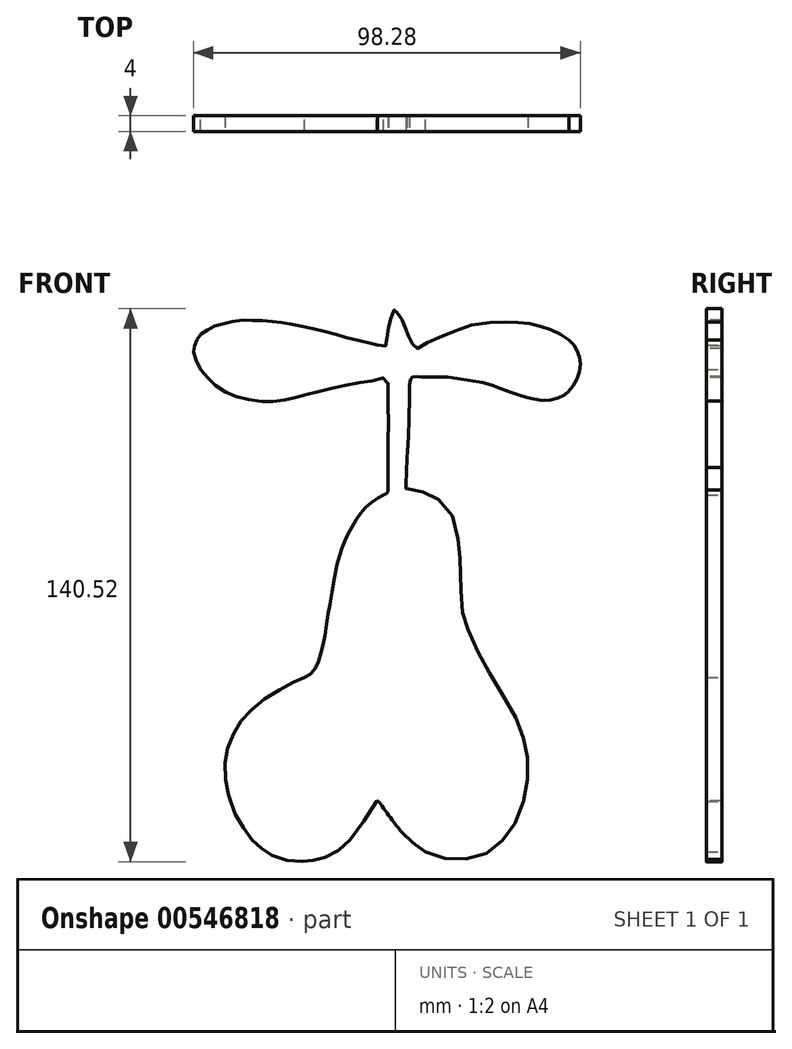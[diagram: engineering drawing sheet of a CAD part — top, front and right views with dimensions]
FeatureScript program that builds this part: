
annotation { "Feature Type Name" : "Feature", "Feature Type Description" : "" }
export const myFeature = defineFeature(function(context is Context, id is Id, definition is map)
    precondition{}
    {
        {
            var Q0;
            Q0=qCreatedBy(makeId("Front.planeOp"),FACE);
            var sketch = newSketch(context, id + "F0", { "sketchPlane" : qUnion([Q0])});
            skFitSpline(sketch, "E0", {"points": [v(-20.35, -65.57) * mm, v(-23.14, -70.04) * mm, v(-26.51, -74.67) * mm, v(-28.55, -76.95) * mm, v(-30.23, -78.14) * mm, v(-32.67, -79.37) * mm, v(-33.78, -79.88) * mm, v(-35.11, -80.2) * mm, v(-36.93, -80.61) * mm, v(-38.53, -80.75) * mm, v(-39.07, -80.8) * mm, v(-40.43, -80.88) * mm, v(-43.22, -80.56) * mm, v(-45.88, -79.83) * mm, v(-47.46, -78.88) * mm, v(-48.54, -78.2) * mm, v(-50.17, -76.95) * mm, v(-51.26, -75.97) * mm, v(-52.29, -74.89) * mm, v(-53.54, -73.2) * mm, v(-55, -71) * mm, v(-56.38, -68.51) * mm, v(-57.66, -64.74) * mm, v(-58.37, -62) * mm, v(-58.72, -59.5) * mm, v(-58.83, -56.87) * mm, v(-58.64, -54.6) * mm, v(-58.23, -52.48) * mm, v(-57.74, -50.77) * mm, v(-56.41, -47.97) * mm, v(-55.22, -45.88) * mm, v(-54.19, -44.58) * mm, v(-52.56, -42.87) * mm, v(-50.44, -40.8) * mm, v(-48.22, -39.2) * mm, v(-45.56, -37.6) * mm, v(-43.3, -36.3) * mm, v(-41.3, -35.27) * mm, v(-39.72, -34.57) * mm, v(-38.58, -34.08) * mm], "startDerivative": vector(-67.21, -112.45) * mm, "endDerivative": vector(58.14, 24.82) * mm});
            skFitSpline(sketch, "E1", {"points": [v(-38.58, -34.08) * mm, v(-37.08, -33.12) * mm, v(-35.5, -31.05) * mm, v(-34.4, -27.64) * mm, v(-33.66, -24.6) * mm, v(-32.78, -19.2) * mm, v(-32.01, -14.78) * mm, v(-30.44, -6) * mm, v(-29.4, -2.35) * mm, v(-28.44, 0.5) * mm, v(-27.37, 2.68) * mm, v(-25.95, 5.33) * mm, v(-24.34, 7.7) * mm, v(-22.5, 9.62) * mm, v(-20.2, 11.35) * mm, v(-18.58, 12.35) * mm], "startDerivative": vector(31.4, 16.8) * mm, "endDerivative": vector(30.53, 18.13) * mm});
            skFitSpline(sketch, "E2", {"points": [v(-18.58, 12.35) * mm, v(-17.6, 12.81) * mm, v(-17.35, 13.9) * mm, v(-17.33, 15.7) * mm], "startDerivative": vector(3.83, 1.07) * mm, "endDerivative": vector(0, 4.79) * mm});
            skFitSpline(sketch, "E3", {"points": [v(-17.33, 15.7) * mm, v(-17.33, 25.86) * mm, v(-17.33, 33.69) * mm, v(-17.33, 38.6) * mm, v(-17.33, 40.37) * mm, v(-17.96, 41.98) * mm, v(-20.9, 41.44) * mm, v(-23.99, 40.9) * mm, v(-29.9, 39.75) * mm, v(-33.54, 38.98) * mm, v(-37.55, 37.91) * mm, v(-40.6, 37.14) * mm, v(-43.8, 36.38) * mm, v(-47.05, 36.07) * mm, v(-50.25, 36.15) * mm, v(-54.7, 36.99) * mm, v(-57.9, 38.06) * mm, v(-60.83, 39.9) * mm, v(-62.95, 41.75) * mm, v(-65.07, 44.2) * mm], "startDerivative": vector(-0.05, 122.05) * mm, "endDerivative": vector(-43.66, 53.5) * mm});
            skFitSpline(sketch, "E4", {"points": [v(-65.07, 44.2) * mm, v(-66.48, 47.5) * mm, v(-66.8, 49.42) * mm, v(-66.26, 50.96) * mm, v(-65.45, 52.58) * mm, v(-64.03, 53.77) * mm, v(-61.86, 55) * mm, v(-59.48, 55.73) * mm, v(-55.44, 56.6) * mm, v(-51.83, 56.64) * mm, v(-48.18, 56.5) * mm, v(-44.86, 56.14) * mm, v(-41.67, 55.6) * mm, v(-36.99, 54.64) * mm, v(-31.15, 53.18) * mm, v(-27.15, 52.08) * mm, v(-21.1, 50.63) * mm, v(-20.06, 50.4) * mm], "startDerivative": vector(-25.5, 55.32) * mm, "endDerivative": vector(22.73, -4.66) * mm});
            skFitSpline(sketch, "E5", {"points": [v(-20.06, 50.4) * mm, v(-18.4, 50.08) * mm, v(-17.84, 50.4) * mm, v(-17.62, 51.98) * mm, v(-17.41, 53.95) * mm, v(-16.93, 56.37) * mm, v(-16.45, 57.73) * mm, v(-15.86, 59.27) * mm, v(-15.68, 59.63) * mm, v(-15.34, 59.02) * mm, v(-14.38, 57.6) * mm, v(-13.67, 56.43) * mm, v(-13.14, 55.3) * mm, v(-12.46, 53.43) * mm, v(-11.68, 51.72) * mm, v(-11.07, 50.4) * mm, v(-10.59, 49.5) * mm, v(-8.24, 50.4) * mm, v(-6.28, 51.56) * mm, v(-1.65, 53.47) * mm, v(4.65, 55.63) * mm, v(11, 56.18) * mm, v(14.55, 56.18) * mm, v(17.52, 55.95) * mm, v(20.12, 55.47) * mm, v(22.93, 54.66) * mm, v(24.48, 54.14) * mm, v(26.65, 52.98) * mm, v(28.52, 51.66) * mm], "startDerivative": vector(58.39, -16.35) * mm, "endDerivative": vector(47.8, -35.82) * mm});
            skFitSpline(sketch, "E6", {"points": [v(28.52, 51.66) * mm, v(29.77, 50.4) * mm, v(30.46, 49.4) * mm, v(31.05, 47.98) * mm, v(31.4, 46.43) * mm, v(31.44, 44.69) * mm, v(31.03, 42.72) * mm, v(30.1, 40.75) * mm, v(29, 39.14) * mm, v(28.1, 38.2) * mm, v(27.35, 37.69) * mm, v(25.94, 37.04) * mm, v(24.07, 36.4) * mm, v(22.02, 36.24) * mm, v(19.64, 36.66) * mm, v(17.98, 37.01) * mm, v(15.63, 37.82) * mm, v(12.87, 38.72) * mm, v(9.72, 39.88) * mm, v(7.12, 40.72) * mm, v(2.03, 41.6) * mm, v(-1.85, 42.17) * mm, v(-4.52, 42.3) * mm], "startDerivative": vector(33.1, -31.28) * mm, "endDerivative": vector(-51.08, 1) * mm});
            skFitSpline(sketch, "E7", {"points": [v(-4.52, 42.3) * mm, v(-6.66, 42.3) * mm, v(-9.72, 42.3) * mm, v(-11.48, 42.04) * mm, v(-11.94, 37.95) * mm, v(-11.98, 35.36) * mm, v(-12.07, 31.59) * mm, v(-12.14, 29.23) * mm, v(-12.44, 22.9) * mm, v(-12.69, 19.33) * mm], "startDerivative": vector(-22.16, 0.28) * mm, "endDerivative": vector(-2.1, -26.63) * mm});
            skFitSpline(sketch, "E8", {"points": [v(-12.69, 19.33) * mm, v(-12.69, 15.84) * mm, v(-12.69, 13.75) * mm, v(-10.61, 13.58) * mm, v(-8.6, 13.07) * mm, v(-6.4, 12.4) * mm, v(-4.86, 11.36) * mm, v(-3.17, 9.9) * mm, v(-1.05, 7) * mm, v(0, 2.84) * mm, v(0.52, 0) * mm, v(0.89, -2.61) * mm, v(0.98, -5.07) * mm, v(1.2, -13.26) * mm, v(1.39, -16.2) * mm, v(1.6, -18.1) * mm, v(2.03, -19.4) * mm, v(3.17, -22.5) * mm, v(4.86, -26.23) * mm, v(6.45, -29.46) * mm, v(8.35, -32.88) * mm, v(10.77, -36.95) * mm, v(11.82, -38.6) * mm, v(14.9, -43.98) * mm, v(16.24, -47.18) * mm, v(17.13, -50.08) * mm, v(17.75, -52.73) * mm, v(18.05, -54.98) * mm, v(18.16, -57.89) * mm, v(17.8, -61.95) * mm, v(17.2, -64.86) * mm, v(16.22, -68.12) * mm, v(14.7, -71.47) * mm, v(13.19, -73.96) * mm, v(11.04, -76.22) * mm, v(9.15, -78.02) * mm, v(5.98, -79.38) * mm, v(3.47, -80.09) * mm, v(0, -80.31) * mm, v(-2.6, -80.09) * mm, v(-5.14, -79.64) * mm, v(-7.83, -78.4) * mm], "startDerivative": vector(8.4, -134.71) * mm, "endDerivative": vector(-111.62, 59.14) * mm});
            skFitSpline(sketch, "E9", {"points": [v(-7.83, -78.4) * mm, v(-12.92, -74.4) * mm, v(-15.97, -70.76) * mm, v(-17.87, -68.21) * mm, v(-19.4, -66.05) * mm, v(-20.06, -65.44) * mm, v(-20.35, -65.57) * mm], "startDerivative": vector(-20.71, 14.7) * mm, "endDerivative": vector(-4.74, -3.72) * mm});
            skSolve(sketch);
        }
        {
            var Q0;
            Q0=makeQuery(id+"F0.imprint","IMPRINT",FACE,{"disambiguationData":[TD([[makeQuery(id+"F0.imprint","IMPRINT",EDGE,{"derivedFrom":sQuery(id+"F0.wireOp",EDGE,"E0")}),-1.0]])]});
            extrude(context, id + "F1", {"entities" : qUnion([Q0]), "depth" : 4 * mm, "offsetDistance" : 25.4 * mm});
        }
    });
